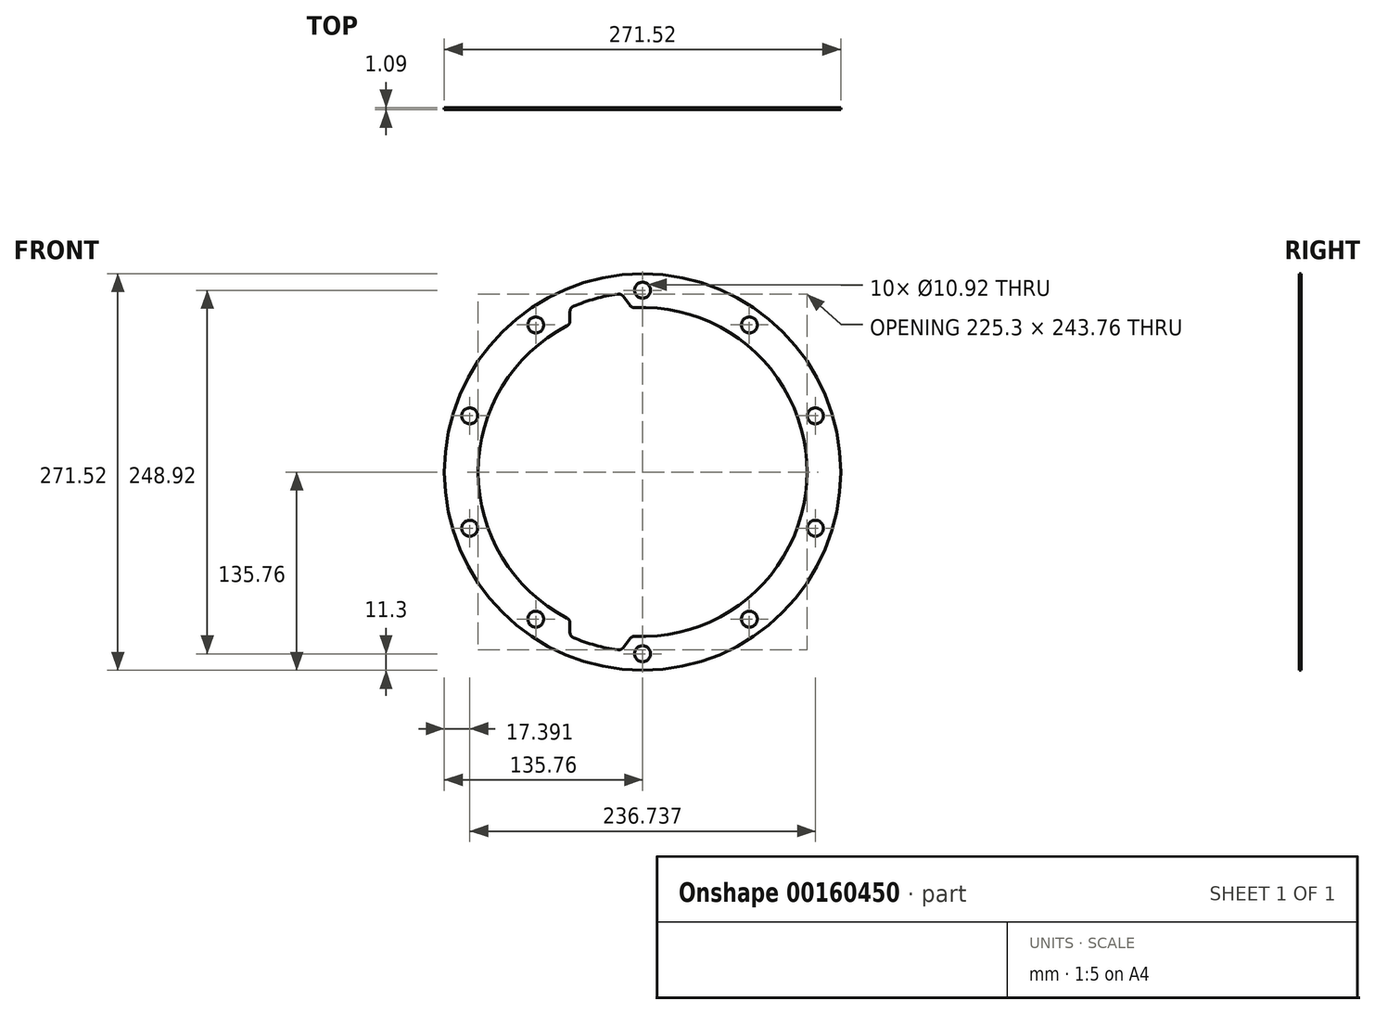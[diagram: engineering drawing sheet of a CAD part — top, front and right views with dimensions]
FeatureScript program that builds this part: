
annotation { "Feature Type Name" : "Feature", "Feature Type Description" : "" }
export const myFeature = defineFeature(function(context is Context, id is Id, definition is map)
    precondition{}
    {
        {
            var Q0;
            Q0=qCreatedBy(makeId("Front.planeOp"),FACE);
            var sketch = newSketch(context, id + "F0", { "sketchPlane" : qUnion([Q0])});
            skCircle(sketch, "E0", {"center": v(0, 0) * mm, "radius": 124.46 * mm, "construction": true});
            skArc(sketch, "E1", {"start": v(-51.79, 100.04) * mm, "mid": v(-112.64, -1.15) * mm, "end": v(-49.73, -101.08) * mm});
            skCircle(sketch, "E2", {"center": v(0, 0) * mm, "radius": 135.76 * mm});
            skLineSegment(sketch, "E3", {"start": v(0, -146.26) * mm, "end": v(0, 137.33) * mm, "construction": true});
            skCircle(sketch, "E4", {"center": v(0, 124.46) * mm, "radius": 5.46 * mm});
            skCircle(sketch, "E5.1.0", {"center": v(-73.16, 100.7) * mm, "radius": 5.46 * mm});
            skCircle(sketch, "E5.2.0", {"center": v(-118.37, 38.46) * mm, "radius": 5.46 * mm});
            skCircle(sketch, "E6.1.3.0", {"center": v(-118.37, -38.46) * mm, "radius": 5.46 * mm});
            skCircle(sketch, "E6.1.4.0", {"center": v(-73.16, -100.7) * mm, "radius": 5.46 * mm});
            skCircle(sketch, "E6.1.5.0", {"center": v(0, -124.46) * mm, "radius": 5.46 * mm});
            skCircle(sketch, "E6.1.6.0", {"center": v(73.16, -100.7) * mm, "radius": 5.46 * mm});
            skCircle(sketch, "E6.1.7.0", {"center": v(118.37, -38.46) * mm, "radius": 5.46 * mm});
            skCircle(sketch, "E6.1.8.0", {"center": v(118.37, 38.46) * mm, "radius": 5.46 * mm});
            skCircle(sketch, "E6.1.9.0", {"center": v(73.16, 100.7) * mm, "radius": 5.46 * mm});
            skLineSegment(sketch, "E7", {"start": v(-13.42, 120.37) * mm, "end": v(-8.62, 114.03) * mm});
            skLineSegment(sketch, "E8", {"start": v(-146.2, 0) * mm, "end": v(165.58, 0) * mm, "construction": true});
            skLineSegment(sketch, "E9", {"start": v(0, 0) * mm, "end": v(-73.16, 100.7) * mm, "construction": true});
            skLineSegment(sketch, "E10", {"start": v(0, 0) * mm, "end": v(-47.97, 147.62) * mm, "construction": true});
            skLineSegment(sketch, "E11", {"start": v(-49.73, 109.9) * mm, "end": v(-49.73, 103.42) * mm});
            skArc(sketch, "E12.trimOffspring", {"start": v(-17, 121.84) * mm, "mid": v(-32.48, 118.61) * mm, "end": v(-47.4, 113.4) * mm});
            skPoint(sketch, "E13.visualSharp", {"position": v(-49.73, 112.39) * mm});
            skArc(sketch, "E13.filletArc", {"start": v(-47.4, 113.4) * mm, "mid": v(-49.1, 112) * mm, "end": v(-49.73, 109.9) * mm});
            skPoint(sketch, "E14.visualSharp", {"position": v(-49.73, 101.08) * mm});
            skArc(sketch, "E14.filletArc", {"start": v(-51.79, 100.04) * mm, "mid": v(-50.29, 101.44) * mm, "end": v(-49.73, 103.42) * mm});
            skPoint(sketch, "E15.visualSharp", {"position": v(-14.76, 122.14) * mm});
            skArc(sketch, "E15.filletArc", {"start": v(-13.42, 120.37) * mm, "mid": v(-15, 121.6) * mm, "end": v(-17, 121.84) * mm});
            skPoint(sketch, "E16.visualSharp", {"position": v(-7.4, 112.4) * mm});
            skArc(sketch, "E16.filletArc", {"start": v(-8.62, 114.03) * mm, "mid": v(-7.2, 112.87) * mm, "end": v(-5.4, 112.52) * mm});
            skArc(sketch, "E17.MirrorCS", {"start": v(-51.79, -100.04) * mm, "mid": v(-50.29, -101.44) * mm, "end": v(-49.73, -103.42) * mm});
            skArc(sketch, "E18.MirrorCS", {"start": v(-13.42, -120.37) * mm, "mid": v(-15, -121.6) * mm, "end": v(-17, -121.84) * mm});
            skArc(sketch, "E19.MirrorCS", {"start": v(-47.4, -113.4) * mm, "mid": v(-49.1, -112) * mm, "end": v(-49.73, -109.9) * mm});
            skArc(sketch, "E20.MirrorCS", {"start": v(-8.62, -114.03) * mm, "mid": v(-7.2, -112.87) * mm, "end": v(-5.4, -112.52) * mm});
            skArc(sketch, "E21.MirrorCS", {"start": v(-17, -121.84) * mm, "mid": v(-32.48, -118.61) * mm, "end": v(-47.4, -113.4) * mm});
            skLineSegment(sketch, "E22.MirrorCS", {"start": v(-49.73, -109.9) * mm, "end": v(-49.73, -103.42) * mm});
            skPoint(sketch, "E23.MirrorP", {"position": v(-49.73, -112.39) * mm});
            skPoint(sketch, "E24.MirrorP", {"position": v(-49.73, -101.08) * mm});
            skPoint(sketch, "E25.MirrorP", {"position": v(-14.76, -122.14) * mm});
            skLineSegment(sketch, "E26.MirrorCS", {"start": v(-13.42, -120.37) * mm, "end": v(-8.62, -114.03) * mm});
            skPoint(sketch, "E27.MirrorP", {"position": v(-7.4, -112.4) * mm});
            skArc(sketch, "E28.trimOffspring", {"start": v(-7.4, -112.4) * mm, "mid": v(112.64, -1) * mm, "end": v(-5.4, 112.52) * mm});
            skSolve(sketch);
        }
        {
            var Q0;
            Q0 = qSketchRegion(id + "F0", true);
            extrude(context, id + "F1", {"entities" : qUnion([Q0]), "depth" : 1.1 * mm});
        }
    });
